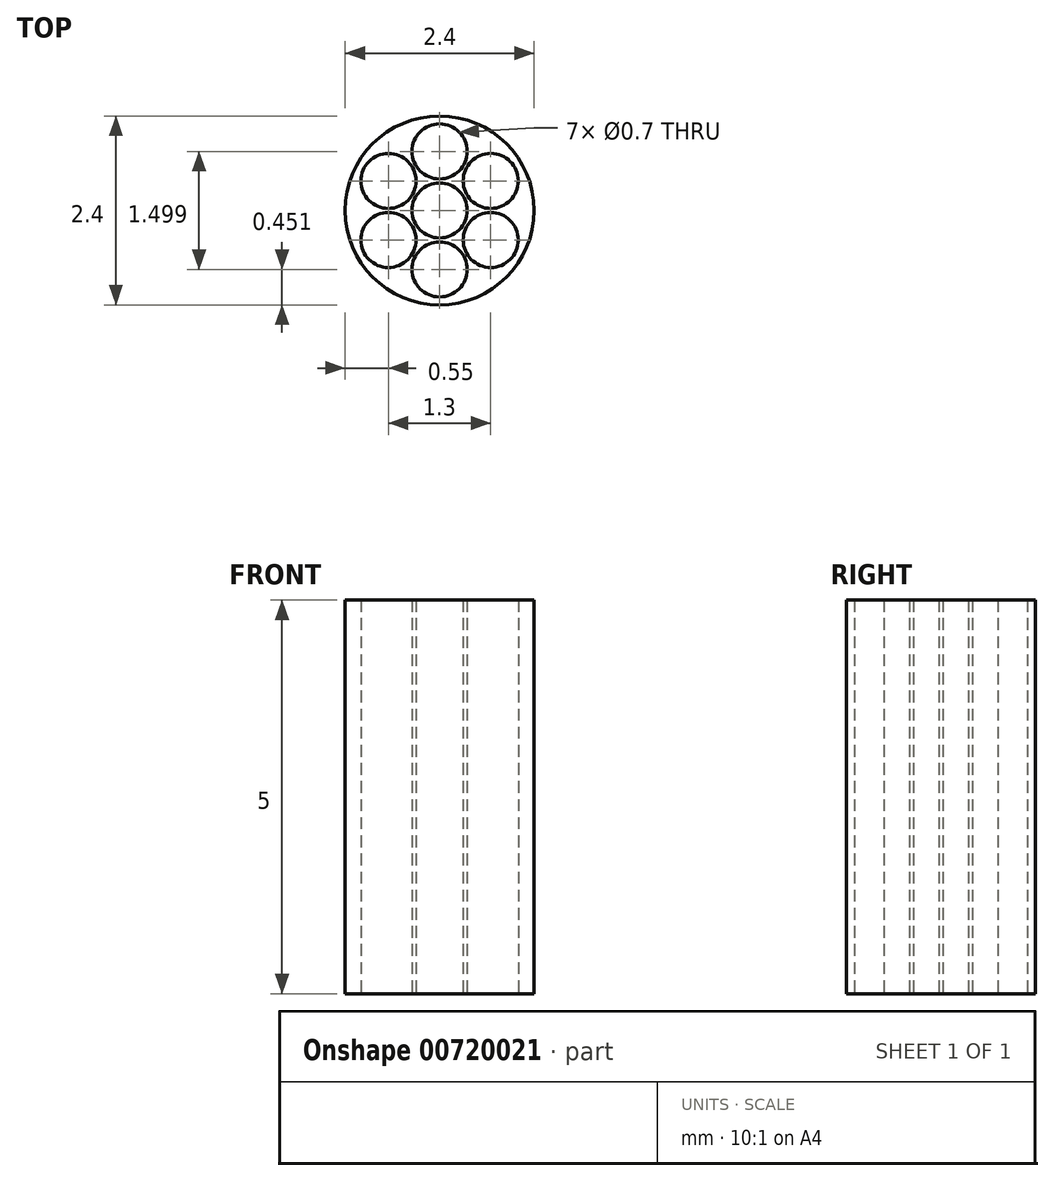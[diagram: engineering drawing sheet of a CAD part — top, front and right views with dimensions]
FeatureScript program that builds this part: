
annotation { "Feature Type Name" : "Feature", "Feature Type Description" : "" }
export const myFeature = defineFeature(function(context is Context, id is Id, definition is map)
    precondition{}
    {
        {
            var Q0;
            Q0=qCreatedBy(makeId("Top.planeOp"),FACE);
            var sketch = newSketch(context, id + "F0", { "sketchPlane" : qUnion([Q0])});
            skCircle(sketch, "E0", {"center": v(0, 0) * mm, "radius": 0.35 * mm});
            skCircle(sketch, "E1", {"center": v(0, 0.75) * mm, "radius": 0.35 * mm});
            skCircle(sketch, "E2", {"center": v(0.65, 0.38) * mm, "radius": 0.35 * mm});
            skCircle(sketch, "E3", {"center": v(0.65, -0.38) * mm, "radius": 0.35 * mm});
            skCircle(sketch, "E4", {"center": v(0, -0.75) * mm, "radius": 0.35 * mm});
            skCircle(sketch, "E5", {"center": v(-0.65, -0.38) * mm, "radius": 0.35 * mm});
            skCircle(sketch, "E6", {"center": v(-0.65, 0.38) * mm, "radius": 0.35 * mm});
            skSolve(sketch);
        }
        {
            var Q0;
            Q0=qCreatedBy(makeId("Top.planeOp"),FACE);
            var sketch = newSketch(context, id + "F1", { "sketchPlane" : qUnion([Q0])});
            skCircle(sketch, "E7", {"center": v(0, 0) * mm, "radius": 1.2 * mm});
            skSolve(sketch);
        }
        {
            var Q0;
            Q0 = qSketchRegion(id + "F1", true);
            extrude(context, id + "F2", {"entities" : qUnion([Q0]), "depth" : 5 * mm, "offsetDistance" : 25 * mm});
        }
        {
            var Q0;
            Q0 = qSketchRegion(id + "F0", true);
            extrude(context, id + "F3", {"entities" : qUnion([Q0]), "operationType" : NewBodyOperationType.REMOVE, "endBound" : BoundingType.THROUGH_ALL, "depth" : 25 * mm, "offsetDistance" : 25 * mm});
        }
    });
